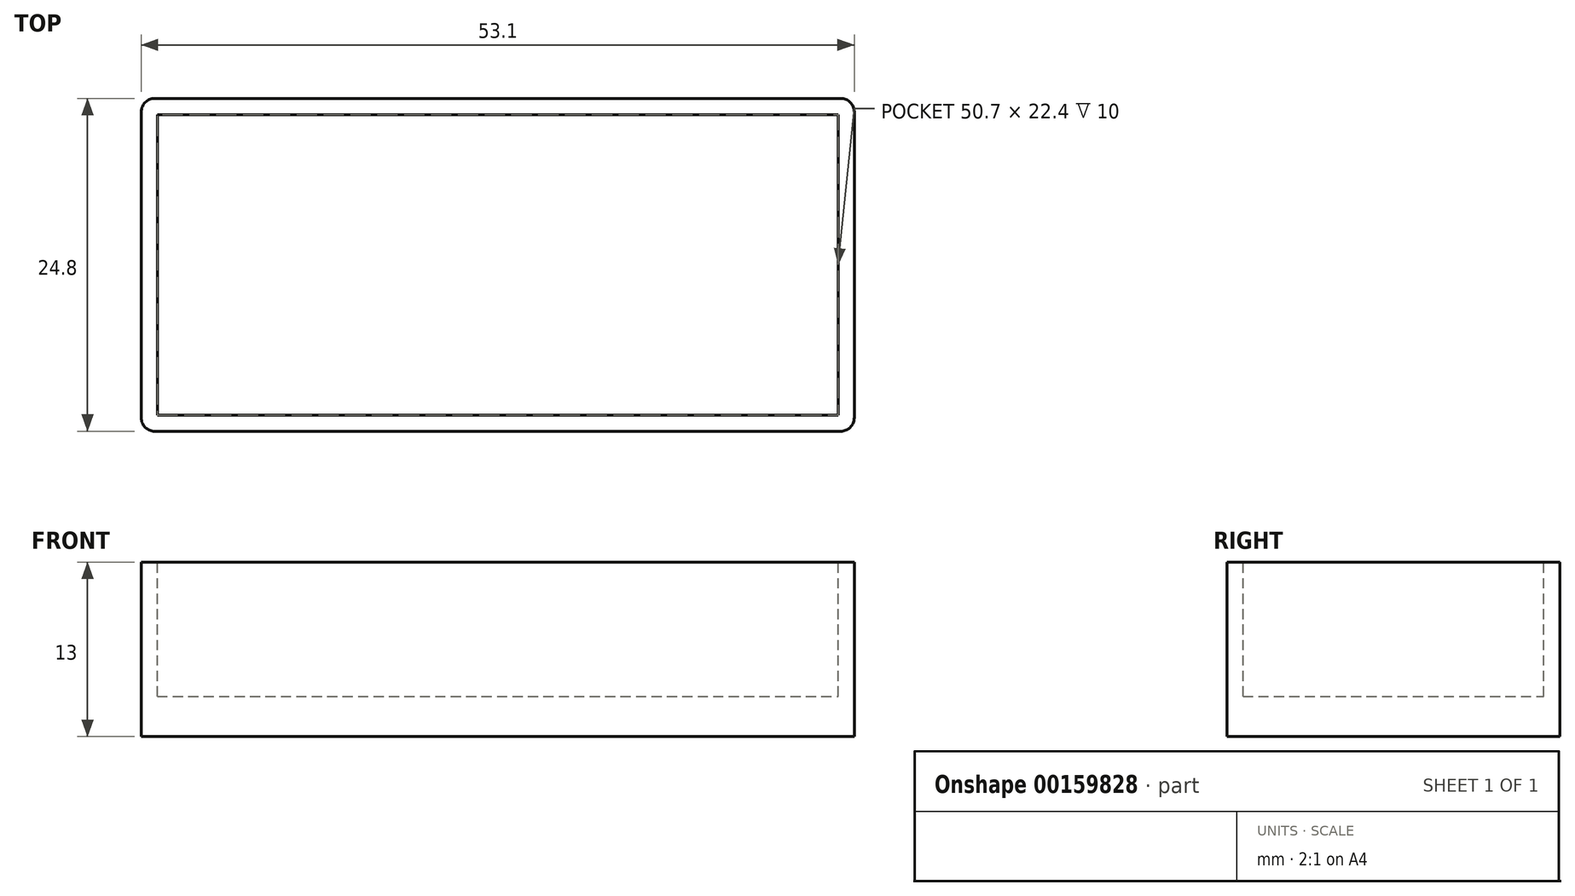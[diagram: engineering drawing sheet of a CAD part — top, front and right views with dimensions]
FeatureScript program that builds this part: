
annotation { "Feature Type Name" : "Feature", "Feature Type Description" : "" }
export const myFeature = defineFeature(function(context is Context, id is Id, definition is map)
    precondition{}
    {
        {
            var Q0;
            Q0=qCreatedBy(makeId("Top.planeOp"),FACE);
            var sketch = newSketch(context, id + "F0", { "sketchPlane" : qUnion([Q0])});
            skLineSegment(sketch, "E0.bottom", {"start": v(0, 0) * mm, "end": v(53.1, 0) * mm});
            skLineSegment(sketch, "E0.top", {"start": v(0, 24.8) * mm, "end": v(53.1, 24.8) * mm});
            skLineSegment(sketch, "E0.left", {"start": v(0, 0) * mm, "end": v(0, 24.8) * mm});
            skLineSegment(sketch, "E0.right", {"start": v(53.1, 0) * mm, "end": v(53.1, 24.8) * mm});
            skSolve(sketch);
        }
        {
            var Q0;
            Q0=makeQuery(id+"F0.imprint","IMPRINT",FACE,{"disambiguationData":[TD([[makeQuery(id+"F0.imprint","IMPRINT",EDGE,{"derivedFrom":sQuery(id+"F0.wireOp",EDGE,"E0.bottom")}),1.0]])]});
            extrude(context, id + "F1", {"entities" : qUnion([Q0]), "depth" : 13 * mm});
        }
        {
            var Q0;
            Q0=makeQuery(id+"F1.opExtrude","SWEPT_EDGE",EDGE,{"disambiguationData":[OSD([sQuery(id+"F0.wireOp",EDGE,"E0.top"),sQuery(id+"F0.wireOp",EDGE,"E0.right")])]});
            var Q1;
            Q1=makeQuery(id+"F1.opExtrude","SWEPT_EDGE",EDGE,{"disambiguationData":[OSD([sQuery(id+"F0.wireOp",EDGE,"E0.bottom"),sQuery(id+"F0.wireOp",EDGE,"E0.right")])]});
            var Q2;
            Q2=makeQuery(id+"F1.opExtrude","SWEPT_EDGE",EDGE,{"disambiguationData":[OSD([sQuery(id+"F0.wireOp",EDGE,"E0.top"),sQuery(id+"F0.wireOp",EDGE,"E0.left")])]});
            var Q3;
            Q3=makeQuery(id+"F1.opExtrude","SWEPT_EDGE",EDGE,{"disambiguationData":[OSD([sQuery(id+"F0.wireOp",EDGE,"E0.bottom"),sQuery(id+"F0.wireOp",EDGE,"E0.left")])]});
            fillet(context, id + "F2", {"entities" : qUnion([Q0, Q1, Q2, Q3]), "radius" : 1 * mm, "tangentPropagation" : true, "allowEdgeOverflow" : false});
        }
        {
            var Q0;
            Q0=makeQuery(id+"F1.opExtrude","CAP_FACE",FACE,{"disambiguationData":[OSD([sQuery(id+"F0.wireOp",EDGE,"E0.bottom"),sQuery(id+"F0.wireOp",EDGE,"E0.top"),sQuery(id+"F0.wireOp",EDGE,"E0.left"),sQuery(id+"F0.wireOp",EDGE,"E0.right")])],"isStart":false});
            var sketch = newSketch(context, id + "F3", { "sketchPlane" : qUnion([Q0])});
            skLineSegment(sketch, "E1.0", {"start": v(1.2, 1.2) * mm, "end": v(1.2, 23.6) * mm});
            skLineSegment(sketch, "E1.1", {"start": v(1.2, 1.2) * mm, "end": v(51.9, 1.2) * mm});
            skLineSegment(sketch, "E1.2", {"start": v(51.9, 1.2) * mm, "end": v(51.9, 23.6) * mm});
            skLineSegment(sketch, "E1.3", {"start": v(1.2, 23.6) * mm, "end": v(51.9, 23.6) * mm});
            skSolve(sketch);
        }
        {
            var Q0;
            Q0=makeQuery(id+"F3.imprint","IMPRINT",FACE,{"disambiguationData":[TD([[makeQuery(id+"F3.imprint","IMPRINT",EDGE,{"derivedFrom":sQuery(id+"F3.wireOp",EDGE,"E1.0")}),-1.0]])]});
            extrude(context, id + "F4", {"entities" : qUnion([Q0]), "operationType" : NewBodyOperationType.REMOVE, "oppositeDirection" : true, "depth" : 10 * mm});
        }
    });
